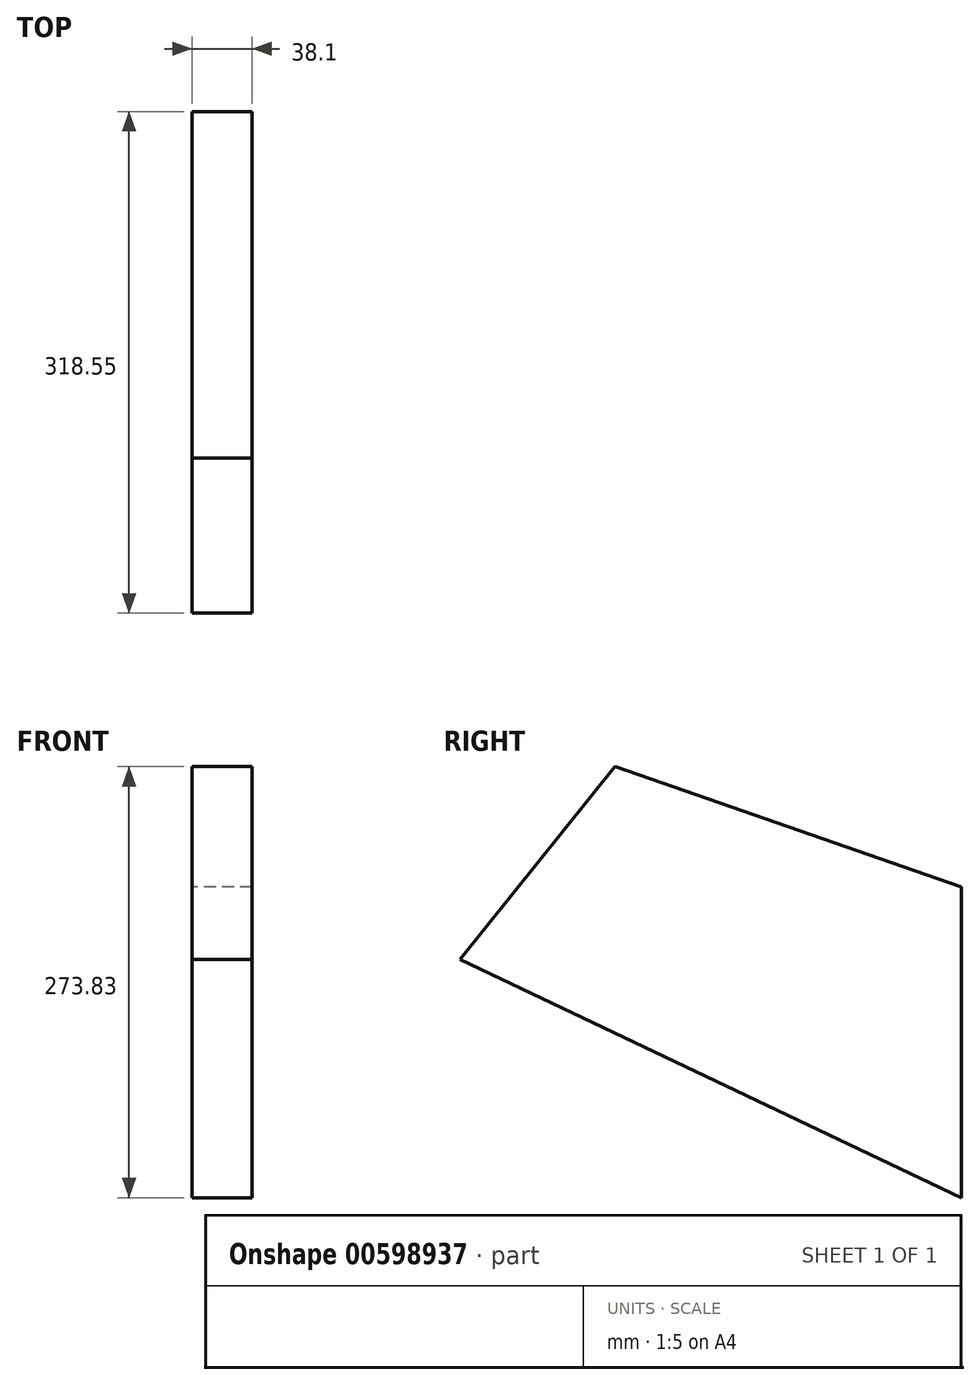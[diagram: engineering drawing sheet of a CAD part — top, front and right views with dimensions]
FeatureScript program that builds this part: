
annotation { "Feature Type Name" : "Feature", "Feature Type Description" : "" }
export const myFeature = defineFeature(function(context is Context, id is Id, definition is map)
    precondition{}
    {
        {
            var Q0;
            Q0=qCreatedBy(makeId("Right.planeOp"),FACE);
            var sketch = newSketch(context, id + "F0", { "sketchPlane" : qUnion([Q0])});
            skLineSegment(sketch, "E0", {"start": v(-66.42, 141.9) * mm, "end": v(-164.99, 19.27) * mm});
            skLineSegment(sketch, "E1", {"start": v(-164.99, 19.27) * mm, "end": v(153.56, -131.93) * mm});
            skLineSegment(sketch, "E2", {"start": v(153.56, -131.93) * mm, "end": v(153.56, 65.48) * mm});
            skLineSegment(sketch, "E3", {"start": v(153.56, 65.48) * mm, "end": v(-66.42, 141.9) * mm});
            skSolve(sketch);
        }
        {
            var Q0;
            Q0=makeQuery(id+"F0.imprint","IMPRINT",FACE,{"disambiguationData":[TD([[makeQuery(id+"F0.imprint","IMPRINT",EDGE,{"derivedFrom":sQuery(id+"F0.wireOp",EDGE,"E0")}),1.0]])]});
            extrude(context, id + "F1", {"entities" : qUnion([Q0]), "endBound" : BoundingType.SYMMETRIC, "depth" : 25.4 * mm, "offsetDistance" : 25.4 * mm});
        }
        {
            var Q0;
            Q0=makeQuery(id+"F1.opExtrude","CAP_FACE",FACE,{"disambiguationData":[OSD([sQuery(id+"F0.wireOp",EDGE,"E0"),sQuery(id+"F0.wireOp",EDGE,"E1"),sQuery(id+"F0.wireOp",EDGE,"E2"),sQuery(id+"F0.wireOp",EDGE,"E3")])],"isStart":false});
            var sketch = newSketch(context, id + "F2", { "sketchPlane" : qUnion([Q0])});
            skSolve(sketch);
        }
        {
            var Q0;
            Q0=makeQuery(id+"F2.imprint","IMPRINT",FACE,{"disambiguationData":[TD([[makeQuery(id+"F2.imprint","IMPRINT",EDGE,{"derivedFrom":makeQuery(id+"F1.opExtrude","CAP_EDGE",EDGE,{"disambiguationData":[OSD([sQuery(id+"F0.wireOp",EDGE,"E0")])],"isStart":false})}),1.0]])]});
            extrude(context, id + "F3", {"entities" : qUnion([Q0]), "operationType" : NewBodyOperationType.ADD, "endBound" : BoundingType.SYMMETRIC, "depth" : 25.4 * mm, "offsetDistance" : 25.4 * mm});
        }
    });
